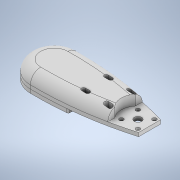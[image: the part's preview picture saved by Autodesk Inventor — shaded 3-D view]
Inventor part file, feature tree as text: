
AUTODESK INVENTOR PART (.ipt)
format: ipt  version: 2020.3 (Build 243373000, 373)  size: 475,136 bytes
history: native  units: mm
features: sketch x10, extrude x9, fillet x2, hole x1
ambient origin geometry x8: Origin, YZ Plane, XZ Plane, XY Plane, X Axis, Y Axis, Z Axis, Center Point
bodies: Body1 (feature_tree)
feature tree (22):
  extrude  "Extrusion2"  Depth=10.0mm TaperAngle=0.0deg
  hole  "Hole1"  [1 undecoded]
  extrude  "Extrusion3"  Depth=5.0mm TaperAngle=0.0deg
  extrude  "Extrusion5"  Depth=2.0mm
  extrude  "Extrusion6"  Depth=11.0mm
  fillet  "Fillet1"  Radius=2.0mm
  extrude  "Extrusion7"  Depth=16.0mm
  extrude  "Extrusion8"  Depth=10.0mm TaperAngle=0.0deg
  extrude  "Extrusion9"  Depth=90.0mm
  extrude  "Extrusion10"  Depth=14.0mm TaperAngle=0.0deg
  extrude  "Extrusion13"  [1 undecoded]
  fillet  "Fillet6"  [1 undecoded]
  sketch  "Sketch1"  dims[d0=142.0mm d1=30.0mm d2=70.0mm d3=30.0mm d4=10.0mm d5=50.0mm d6=45.0mm d7=45.0mm d8=45.0mm d9=45.0mm d12=5.0mm d13=0.0mm]
  sketch  "Sketch2"  dims[d15=40.0mm d16=20.0mm d17=360.0deg d18=3.0mm d19=3.0mm d20=3.0mm d21=3.0mm d22=3.0mm d23=6.0mm d24=5.6mm d25=3.2mm d26=90.0deg d27=8.0mm d28=20.594885mm d29=0.0mm d30=0.0mm]
  sketch  "Sketch3"  dims[d31=5.5mm d38=5.0mm d39=0.0mm]
  sketch  "Sketch5"  dims[d40=5.0mm d41=0.0mm d42=2.0mm]
  sketch  "Sketch6"  dims[d44=5.0mm d45=0.0mm d46=11.0mm d47=2.0mm d48=0.0mm]
  sketch  "Sketch7"  dims[d51=2.0mm d52=0.0mm d53=16.0mm]
  sketch  "Sketch8"  dims[d54=10.0mm d55=45.0mm d56=9.8mm d57=9.8mm d58=9.8mm d59=1.0mm d60=2.0mm d61=2.0mm d62=2.0mm d63=2.0mm d64=2.0mm d65=9.8mm d66=10.0mm d67=0.0mm]
  sketch  "Sketch9"  dims[d68=35.0mm d69=90.0mm]
  sketch  "Sketch10"  dims[d78=45.0mm d79=14.0mm d80=0.0mm]
  sketch  "Sketch11"  dims[d83=14.0mm]
note: 3 required parameter values undecoded (feature->parameter linkage not recoverable at this tier; creation-order binding heuristic only, values carry confidence <= 0.55)
